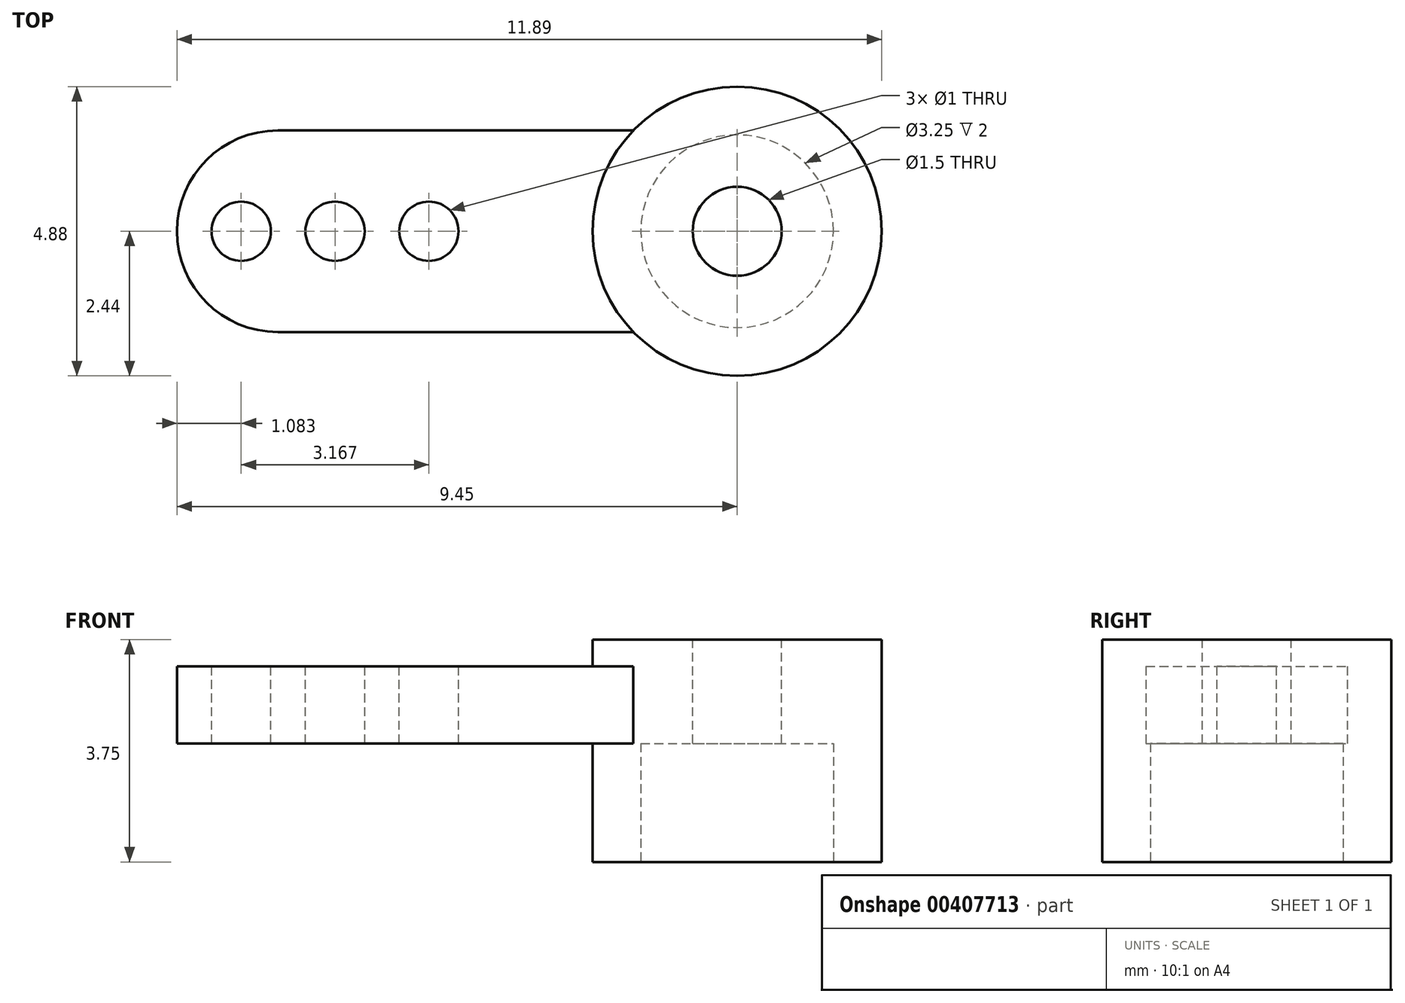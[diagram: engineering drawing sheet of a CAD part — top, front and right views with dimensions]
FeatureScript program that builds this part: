
annotation { "Feature Type Name" : "Feature", "Feature Type Description" : "" }
export const myFeature = defineFeature(function(context is Context, id is Id, definition is map)
    precondition{}
    {
        {
            var Q0;
            Q0=qCreatedBy(makeId("Top.planeOp"),FACE);
            var sketch = newSketch(context, id + "F0", { "sketchPlane" : qUnion([Q0])});
            skCircle(sketch, "E0", {"center": v(0, 0) * mm, "radius": 2.44 * mm});
            skSolve(sketch);
        }
        {
            var Q0;
            Q0 = qSketchRegion(id + "F0", true);
            extrude(context, id + "F1", {"entities" : qUnion([Q0]), "depth" : 3.75 * mm});
        }
        {
            var Q0;
            Q0=makeQuery(id+"F1.opExtrude","CAP_FACE",FACE,{"disambiguationData":[OSD([sQuery(id+"F0.wireOp",EDGE,"E0")])],"isStart":true});
            var sketch = newSketch(context, id + "F2", { "sketchPlane" : qUnion([Q0])});
            skCircle(sketch, "E1", {"center": v(0, 0) * mm, "radius": 1.63 * mm});
            skSolve(sketch);
        }
        {
            var Q0;
            Q0 = qSketchRegion(id + "F2", true);
            extrude(context, id + "F3", {"entities" : qUnion([Q0]), "operationType" : NewBodyOperationType.REMOVE, "oppositeDirection" : true, "depth" : 2 * mm});
        }
        {
            var Q0;
            Q0=makeQuery(id+"F1.opExtrude","CAP_FACE",FACE,{"disambiguationData":[OSD([sQuery(id+"F0.wireOp",EDGE,"E0")])],"isStart":true});
            cPlane(context, id + "F4", {"entities" : qUnion([Q0]), "cplaneType" : CPlaneType.OFFSET, "offset" : 2 * mm, "oppositeDirection" : true, "width" : 150 * mm, "height" : 150 * mm});
        }
        {
            var Q0;
            Q0=qCreatedBy(id+"F4.planeOp",FACE);
            var sketch = newSketch(context, id + "F5", { "sketchPlane" : qUnion([Q0])});
            skLineSegment(sketch, "E2.bottom", {"start": v(-1.75, -1.7) * mm, "end": v(-7.75, -1.7) * mm});
            skLineSegment(sketch, "E2.top", {"start": v(-1.75, 1.7) * mm, "end": v(-7.75, 1.7) * mm});
            skLineSegment(sketch, "E2.left", {"start": v(-1.75, -1.7) * mm, "end": v(-1.75, 1.7) * mm});
            skLineSegment(sketch, "E3", {"start": v(-1.75, 0) * mm, "end": v(0, 0) * mm, "construction": true});
            skArc(sketch, "E4", {"start": v(-7.75, 1.7) * mm, "mid": v(-9.45, 0) * mm, "end": v(-7.75, -1.7) * mm});
            skSolve(sketch);
        }
        {
            var Q0;
            Q0 = qSketchRegion(id + "F5", true);
            extrude(context, id + "F6", {"entities" : qUnion([Q0]), "operationType" : NewBodyOperationType.ADD, "oppositeDirection" : true, "depth" : 1.3 * mm});
        }
        {
            var Q0;
            Q0=makeQuery(id+"F1.opExtrude","CAP_FACE",FACE,{"disambiguationData":[OSD([sQuery(id+"F0.wireOp",EDGE,"E0")])],"isStart":false});
            var sketch = newSketch(context, id + "F7", { "sketchPlane" : qUnion([Q0])});
            skCircle(sketch, "E5", {"center": v(0, 0) * mm, "radius": 0.75 * mm});
            skSolve(sketch);
        }
        {
            var Q0;
            Q0 = qSketchRegion(id + "F7", true);
            extrude(context, id + "F8", {"entities" : qUnion([Q0]), "operationType" : NewBodyOperationType.REMOVE, "oppositeDirection" : true, "depth" : 25 * mm});
        }
        {
            var Q0;
            Q0=makeQuery(id+"F6.opExtrude","CAP_FACE",FACE,{"disambiguationData":[OSD([sQuery(id+"F5.wireOp",EDGE,"E2.bottom"),sQuery(id+"F5.wireOp",EDGE,"E2.top"),sQuery(id+"F5.wireOp",EDGE,"E2.left"),sQuery(id+"F5.wireOp",EDGE,"E4")])],"isStart":false});
            var sketch = newSketch(context, id + "F9", { "sketchPlane" : qUnion([Q0])});
            skCircle(sketch, "E6", {"center": v(-8.37, 0) * mm, "radius": 0.5 * mm});
            skCircle(sketch, "E7", {"center": v(-6.78, 0) * mm, "radius": 0.5 * mm});
            skCircle(sketch, "E8", {"center": v(-5.2, 0) * mm, "radius": 0.5 * mm});
            skLineSegment(sketch, "E9", {"start": v(-9.45, 0) * mm, "end": v(-8.87, 0) * mm, "construction": true});
            skLineSegment(sketch, "E10", {"start": v(-7.87, 0) * mm, "end": v(-7.28, 0) * mm, "construction": true});
            skLineSegment(sketch, "E11", {"start": v(-6.28, 0) * mm, "end": v(-5.7, 0) * mm, "construction": true});
            skSolve(sketch);
        }
        {
            var Q0;
            Q0 = qSketchRegion(id + "F9", true);
            var Q1;
            Q1=makeQuery(id+"F6.opExtrude","CAP_FACE",FACE,{"disambiguationData":[OSD([sQuery(id+"F5.wireOp",EDGE,"E2.bottom"),sQuery(id+"F5.wireOp",EDGE,"E2.top"),sQuery(id+"F5.wireOp",EDGE,"E2.left"),sQuery(id+"F5.wireOp",EDGE,"E4")])],"isStart":true});
            extrude(context, id + "F10", {"entities" : qUnion([Q0]), "operationType" : NewBodyOperationType.REMOVE, "endBound" : BoundingType.UP_TO_SURFACE, "oppositeDirection" : true, "endBoundEntityFace" : qUnion([Q1]), "depth" : 25 * mm});
        }
    });
